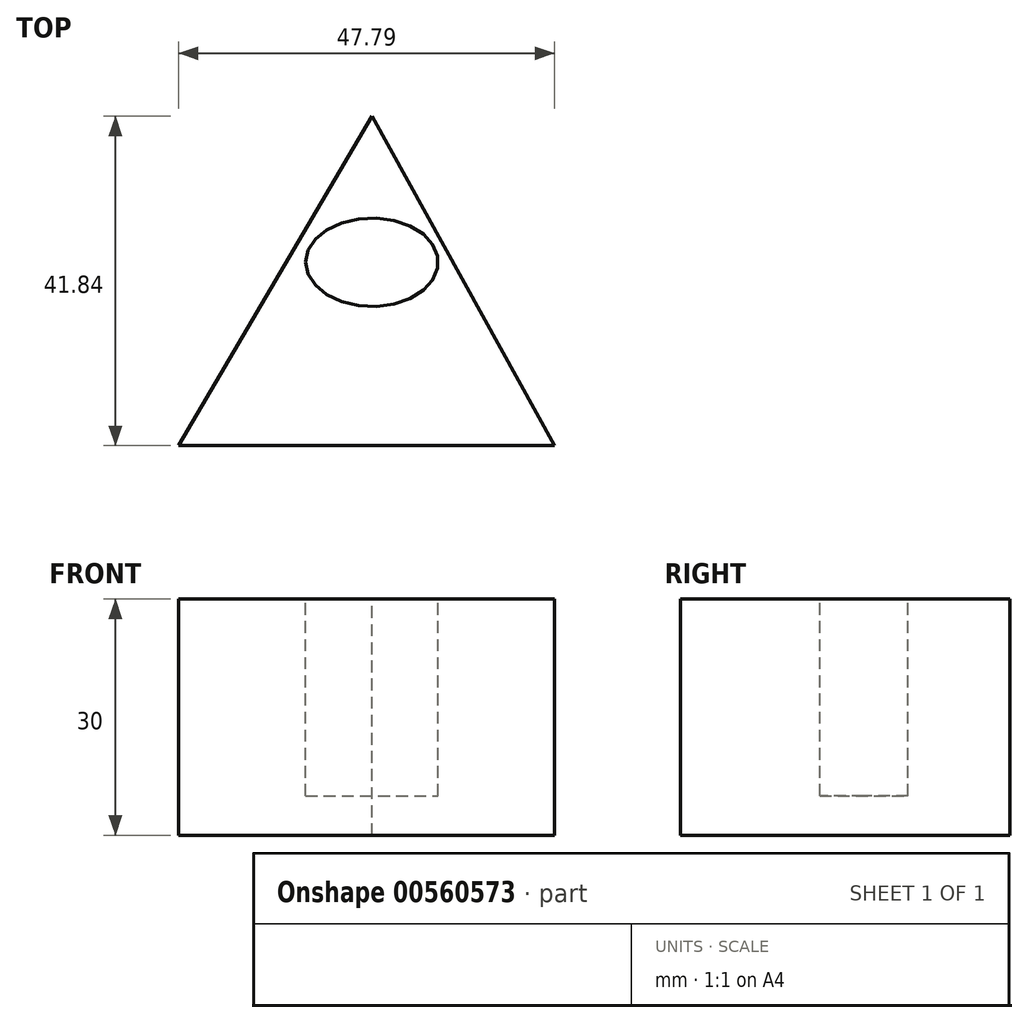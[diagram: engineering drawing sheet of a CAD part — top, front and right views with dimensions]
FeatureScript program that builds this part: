
annotation { "Feature Type Name" : "Feature", "Feature Type Description" : "" }
export const myFeature = defineFeature(function(context is Context, id is Id, definition is map)
    precondition{}
    {
        {
            var Q0;
            Q0=qCreatedBy(makeId("Top.planeOp"),FACE);
            var sketch = newSketch(context, id + "F0", { "sketchPlane" : qUnion([Q0])});
            skLineSegment(sketch, "E0", {"start": v(-24.59, -10.6) * mm, "end": v(23.2, -10.6) * mm});
            skLineSegment(sketch, "E1", {"start": v(-24.59, -10.6) * mm, "end": v(0, 31.23) * mm});
            skLineSegment(sketch, "E2", {"start": v(0, 31.23) * mm, "end": v(23.2, -10.6) * mm});
            skSolve(sketch);
        }
        {
            var Q0;
            Q0=makeQuery(id+"F0.imprint","IMPRINT",FACE,{"disambiguationData":[TD([[makeQuery(id+"F0.imprint","IMPRINT",EDGE,{"derivedFrom":sQuery(id+"F0.wireOp",EDGE,"E0")}),1.0]])]});
            extrude(context, id + "F1", {"entities" : qUnion([Q0]), "oppositeDirection" : true, "depth" : 30 * mm, "offsetDistance" : 25.4 * mm});
        }
        {
            var Q0;
            Q0=makeQuery(id+"F1.opExtrude","CAP_FACE",FACE,{"disambiguationData":[OSD([sQuery(id+"F0.wireOp",EDGE,"E0"),sQuery(id+"F0.wireOp",EDGE,"E1"),sQuery(id+"F0.wireOp",EDGE,"E2")])],"isStart":true});
            extrude(context, id + "F2", {"entities" : qUnion([Q0]), "operationType" : NewBodyOperationType.ADD, "oppositeDirection" : true, "depth" : 3 * mm, "offsetDistance" : 25.4 * mm});
        }
        {
            var Q0;
            Q0=makeQuery(id+"F1.opExtrude","CAP_FACE",FACE,{"disambiguationData":[OSD([sQuery(id+"F0.wireOp",EDGE,"E0"),sQuery(id+"F0.wireOp",EDGE,"E1"),sQuery(id+"F0.wireOp",EDGE,"E2")])],"isStart":true});
            var sketch = newSketch(context, id + "F3", { "sketchPlane" : qUnion([Q0])});
            skEllipse(sketch, "E3", {"center": v(0, 12.7) * mm, "majorRadius": 8.41 * mm, "minorRadius": 5.62 * mm, "majorAxis": v(-1, 0)});
            skSolve(sketch);
        }
        {
            var Q0;
            Q0=makeQuery(id+"F3.imprint","IMPRINT",FACE,{"disambiguationData":[TD([[makeQuery(id+"F3.imprint","IMPRINT",EDGE,{"derivedFrom":sQuery(id+"F3.wireOp",EDGE,"E3")}),1.0]])]});
            extrude(context, id + "F4", {"entities" : qUnion([Q0]), "operationType" : NewBodyOperationType.REMOVE, "oppositeDirection" : true, "depth" : 25 * mm, "offsetDistance" : 25 * mm});
        }
    });
